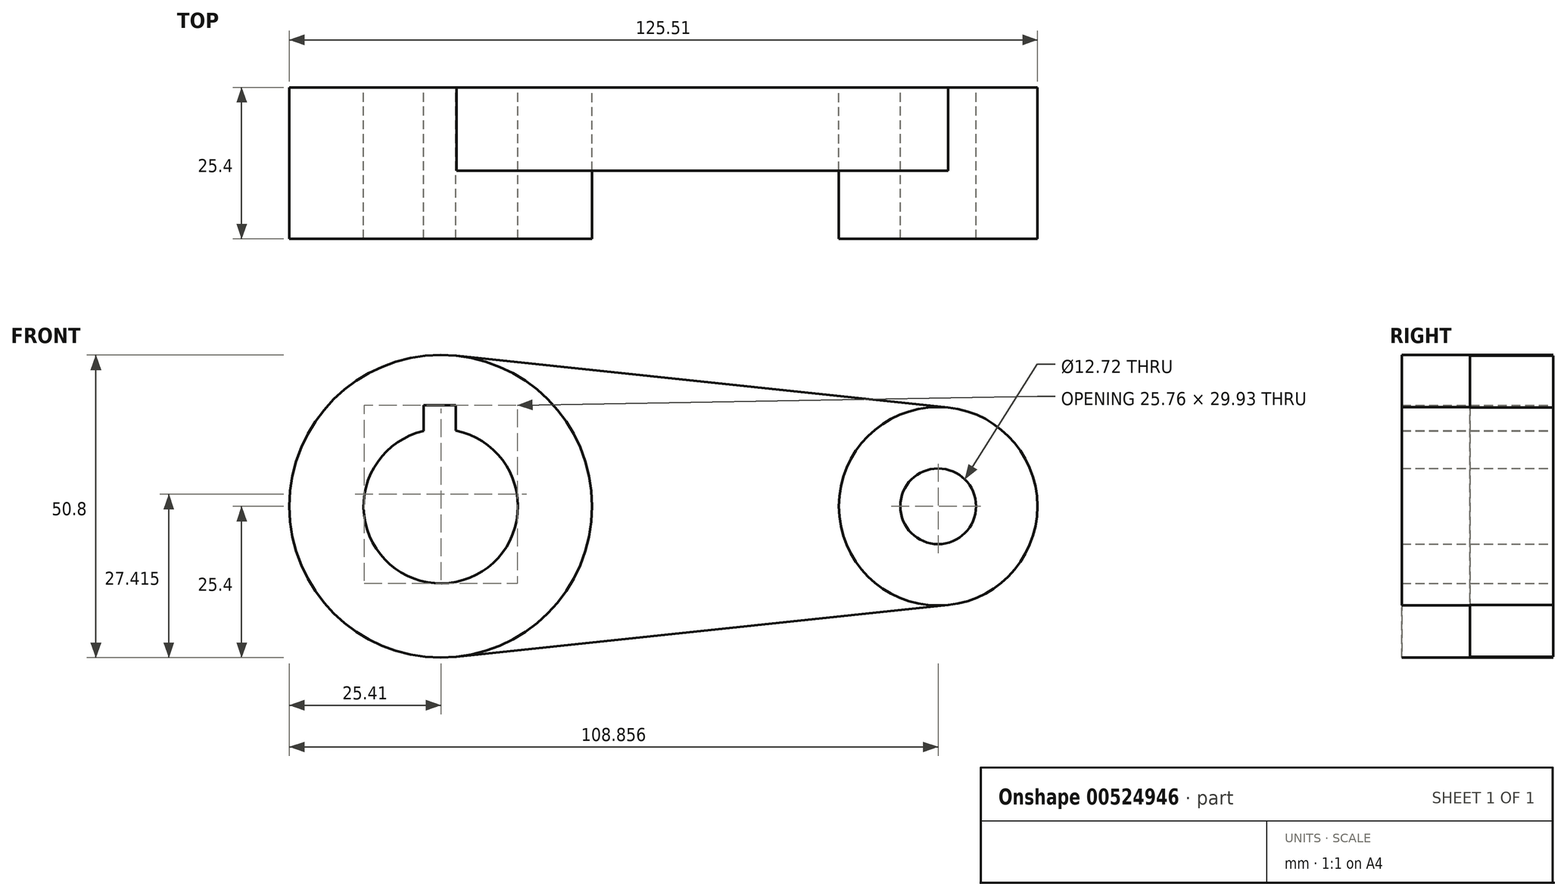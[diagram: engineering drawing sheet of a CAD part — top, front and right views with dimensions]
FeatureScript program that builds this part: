
annotation { "Feature Type Name" : "Feature", "Feature Type Description" : "" }
export const myFeature = defineFeature(function(context is Context, id is Id, definition is map)
    precondition{}
    {
        {
            var Q0;
            Q0=qCreatedBy(makeId("Front.planeOp"),FACE);
            var sketch = newSketch(context, id + "F0", { "sketchPlane" : qUnion([Q0])});
            skCircle(sketch, "E0", {"center": v(-50.08, 0) * mm, "radius": 25.4 * mm});
            skCircle(sketch, "E1", {"center": v(33.39, 0) * mm, "radius": 16.66 * mm});
            skLineSegment(sketch, "E2", {"start": v(35.05, -16.57) * mm, "end": v(-47.42, -25.26) * mm});
            skLineSegment(sketch, "E3", {"start": v(-47.42, 25.26) * mm, "end": v(35.05, 16.57) * mm});
            skCircle(sketch, "E4", {"center": v(-50.08, 0) * mm, "radius": 12.95 * mm});
            skCircle(sketch, "E5", {"center": v(33.39, 0) * mm, "radius": 6.36 * mm});
            skLineSegment(sketch, "E6", {"start": v(-47.54, 12.7) * mm, "end": v(-47.54, 16.98) * mm});
            skLineSegment(sketch, "E7", {"start": v(-47.54, 16.98) * mm, "end": v(-52.96, 16.98) * mm});
            skLineSegment(sketch, "E8", {"start": v(-52.96, 16.98) * mm, "end": v(-52.96, 12.63) * mm});
            skSolve(sketch);
        }
        {
            var Q0;
            {var subQ0=sQuery(id+"F0.wireOp",EDGE,"E6");Q0=makeQuery(id+"F0.imprint","IMPRINT",FACE,{"disambiguationData":[TD([[makeQuery(id+"F0.imprint","IMPRINT",EDGE,{"derivedFrom":subQ0}),-1.0]])]});}
            extrude(context, id + "F1", {"entities" : qUnion([Q0]), "depth" : 25.4 * mm, "offsetDistance" : 25.4 * mm});
        }
        {
            var Q0;
            Q0=makeQuery(id+"F0.imprint","IMPRINT",FACE,{"disambiguationData":[TD([[makeQuery(id+"F0.imprint","IMPRINT",EDGE,{"derivedFrom":sQuery(id+"F0.wireOp",EDGE,"E5")}),-1.0]])]});
            extrude(context, id + "F2", {"entities" : qUnion([Q0]), "depth" : 25.4 * mm, "offsetDistance" : 25.4 * mm});
        }
        {
            var Q0;
            {var subQ0=sQuery(id+"F0.wireOp",EDGE,"E2");Q0=makeQuery(id+"F0.imprint","IMPRINT",FACE,{"disambiguationData":[TD([[makeQuery(id+"F0.imprint","IMPRINT",EDGE,{"derivedFrom":subQ0}),-1.0]])]});}
            extrude(context, id + "F3", {"entities" : qUnion([Q0]), "depth" : 13.97 * mm, "offsetDistance" : 25.4 * mm});
        }
    });
